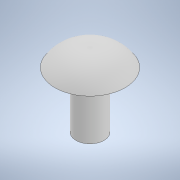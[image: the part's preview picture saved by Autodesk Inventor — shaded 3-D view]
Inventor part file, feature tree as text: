
AUTODESK INVENTOR PART (.ipt)
format: ipt  version: 2020 (Build 240168000, 168)  size: 119,808 bytes
history: native  units: in
note: dims shown in document units (in); Inventor stores cm internally (conversion verified against a paired STEP export)
features: revolve x1, sketch x1
ambient origin geometry x8: Origin, YZ Plane, XZ Plane, XY Plane, X Axis, Y Axis, Z Axis, Center Point
bodies: Solid1 (feature_tree)
feature tree (2):
  revolve  "Revolution1"  [1 undecoded]
  sketch  "Sketch1"  dims[d0=0.325in d1=0.25in d2=0.1562in d3=0.1562in d4=0.0625in d5=90.0deg]
note: 1 required parameter value undecoded (feature->parameter linkage not recoverable at this tier; creation-order binding heuristic only, values carry confidence <= 0.55)
